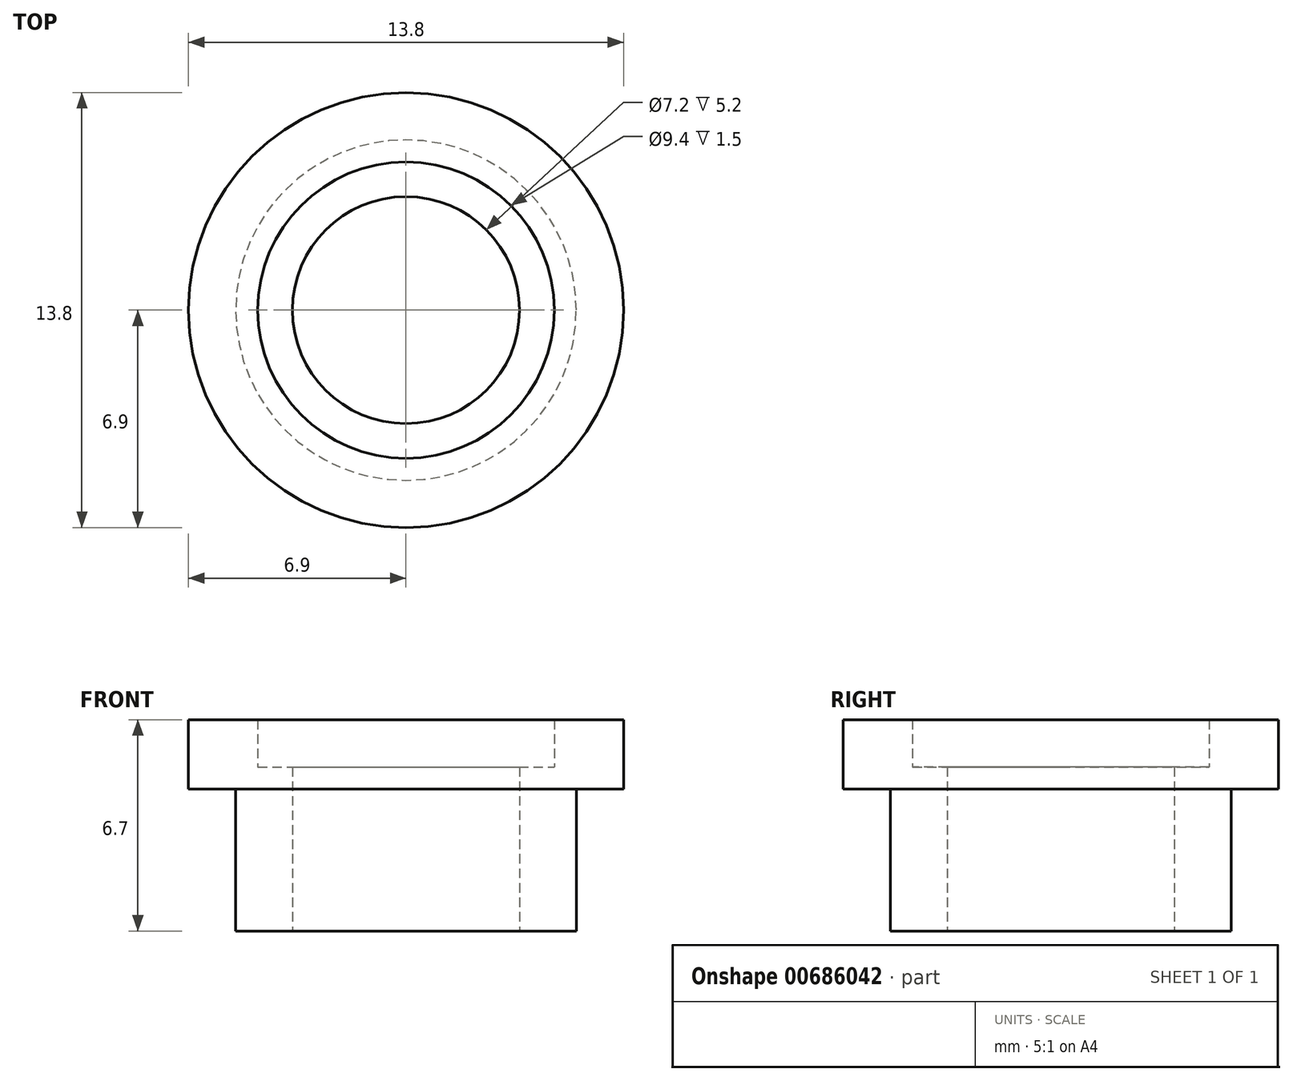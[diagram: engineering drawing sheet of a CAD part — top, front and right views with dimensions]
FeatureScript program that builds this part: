
annotation { "Feature Type Name" : "Feature", "Feature Type Description" : "" }
export const myFeature = defineFeature(function(context is Context, id is Id, definition is map)
    precondition{}
    {
        {
            var Q0;
            Q0=qCreatedBy(makeId("Front.planeOp"),FACE);
            var sketch = newSketch(context, id + "F0", { "sketchPlane" : qUnion([Q0])});
            skLineSegment(sketch, "E0", {"start": v(0, 0) * mm, "end": v(-5.4, 0) * mm});
            skLineSegment(sketch, "E1", {"start": v(-5.4, 0) * mm, "end": v(-5.4, 4.5) * mm});
            skLineSegment(sketch, "E2", {"start": v(-5.4, 4.5) * mm, "end": v(-6.9, 4.5) * mm});
            skLineSegment(sketch, "E3", {"start": v(-6.9, 4.5) * mm, "end": v(-6.9, 6.7) * mm});
            skLineSegment(sketch, "E4", {"start": v(-6.9, 6.7) * mm, "end": v(-4.7, 6.7) * mm});
            skLineSegment(sketch, "E5", {"start": v(-4.7, 6.7) * mm, "end": v(-4.7, 5.2) * mm});
            skLineSegment(sketch, "E6", {"start": v(-4.7, 5.2) * mm, "end": v(-3.6, 5.2) * mm});
            skLineSegment(sketch, "E7", {"start": v(-3.6, 5.2) * mm, "end": v(-3.6, 0) * mm});
            skLineSegment(sketch, "E8", {"start": v(0, 0) * mm, "end": v(0, 2.48) * mm});
            skLineSegment(sketch, "E9.MirrorCS", {"start": v(3.6, 5.2) * mm, "end": v(3.6, 0) * mm});
            skLineSegment(sketch, "E10.MirrorCS", {"start": v(0, 0) * mm, "end": v(5.4, 0) * mm});
            skLineSegment(sketch, "E11.MirrorCS", {"start": v(5.4, 0) * mm, "end": v(5.4, 4.5) * mm});
            skLineSegment(sketch, "E12.MirrorCS", {"start": v(4.7, 5.2) * mm, "end": v(3.6, 5.2) * mm});
            skLineSegment(sketch, "E13.MirrorCS", {"start": v(5.4, 4.5) * mm, "end": v(6.9, 4.5) * mm});
            skLineSegment(sketch, "E14.MirrorCS", {"start": v(6.9, 4.5) * mm, "end": v(6.9, 6.7) * mm});
            skLineSegment(sketch, "E15.MirrorCS", {"start": v(4.7, 6.7) * mm, "end": v(4.7, 5.2) * mm});
            skLineSegment(sketch, "E16.MirrorCS", {"start": v(6.9, 6.7) * mm, "end": v(4.7, 6.7) * mm});
            skSolve(sketch);
        }
        {
            var Q0;
            {var subQ0=sQuery(id+"F0.wireOp",EDGE,"E1");Q0=makeQuery(id+"F0.imprint","IMPRINT",FACE,{"disambiguationData":[TD([[makeQuery(id+"F0.imprint","IMPRINT",EDGE,{"derivedFrom":subQ0}),-1.0]])]});}
            var Q1;
            Q1=sQuery(id+"F0.wireOp",EDGE,"E8");
            revolve(context, id + "F1", {"entities" : qUnion([Q0]), "axis" : qUnion([Q1]), "revolveType" : RevolveType.FULL});
        }
    });
